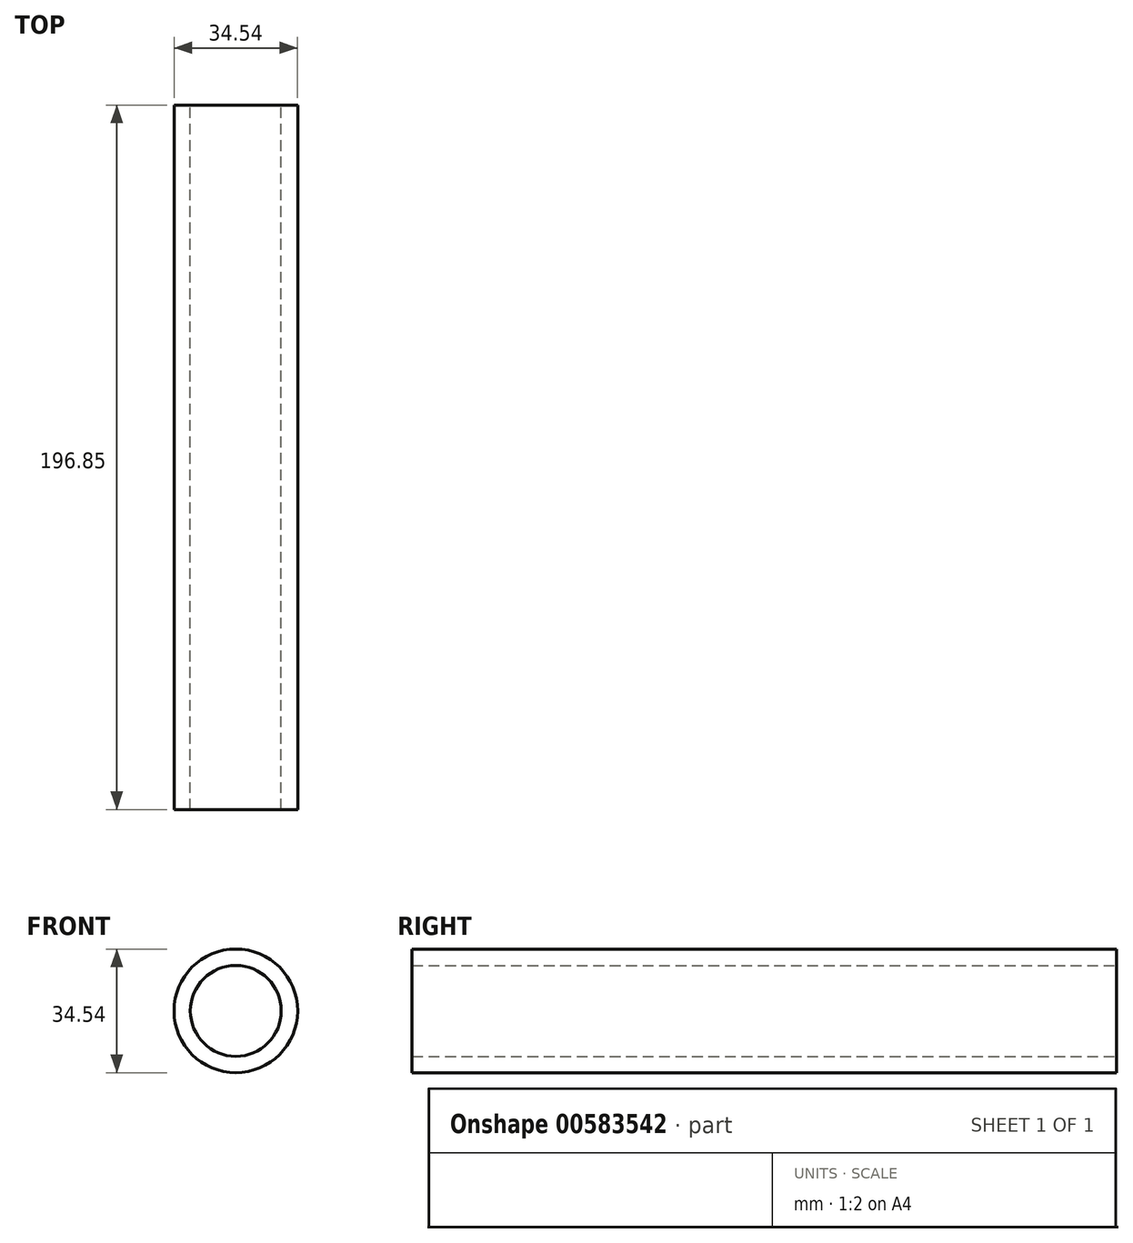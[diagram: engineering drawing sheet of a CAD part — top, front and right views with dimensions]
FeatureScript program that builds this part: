
annotation { "Feature Type Name" : "Feature", "Feature Type Description" : "" }
export const myFeature = defineFeature(function(context is Context, id is Id, definition is map)
    precondition{}
    {
        {
            var Q0;
            Q0=qCreatedBy(makeId("Front.planeOp"),FACE);
            var sketch = newSketch(context, id + "F0", { "sketchPlane" : qUnion([Q0])});
            skCircle(sketch, "E0", {"center": v(0, 0) * mm, "radius": 17.27 * mm});
            skCircle(sketch, "E1", {"center": v(0, 0) * mm, "radius": 12.7 * mm});
            skSolve(sketch);
        }
        {
            var Q0;
            Q0=makeQuery(id+"F0.imprint","IMPRINT",FACE,{"disambiguationData":[TD([[makeQuery(id+"F0.imprint","IMPRINT",EDGE,{"derivedFrom":sQuery(id+"F0.wireOp",EDGE,"E0")}),1.0]])]});
            extrude(context, id + "F1", {"entities" : qUnion([Q0]), "depth" : 196.85 * mm, "offsetDistance" : 25.4 * mm});
        }
    });
